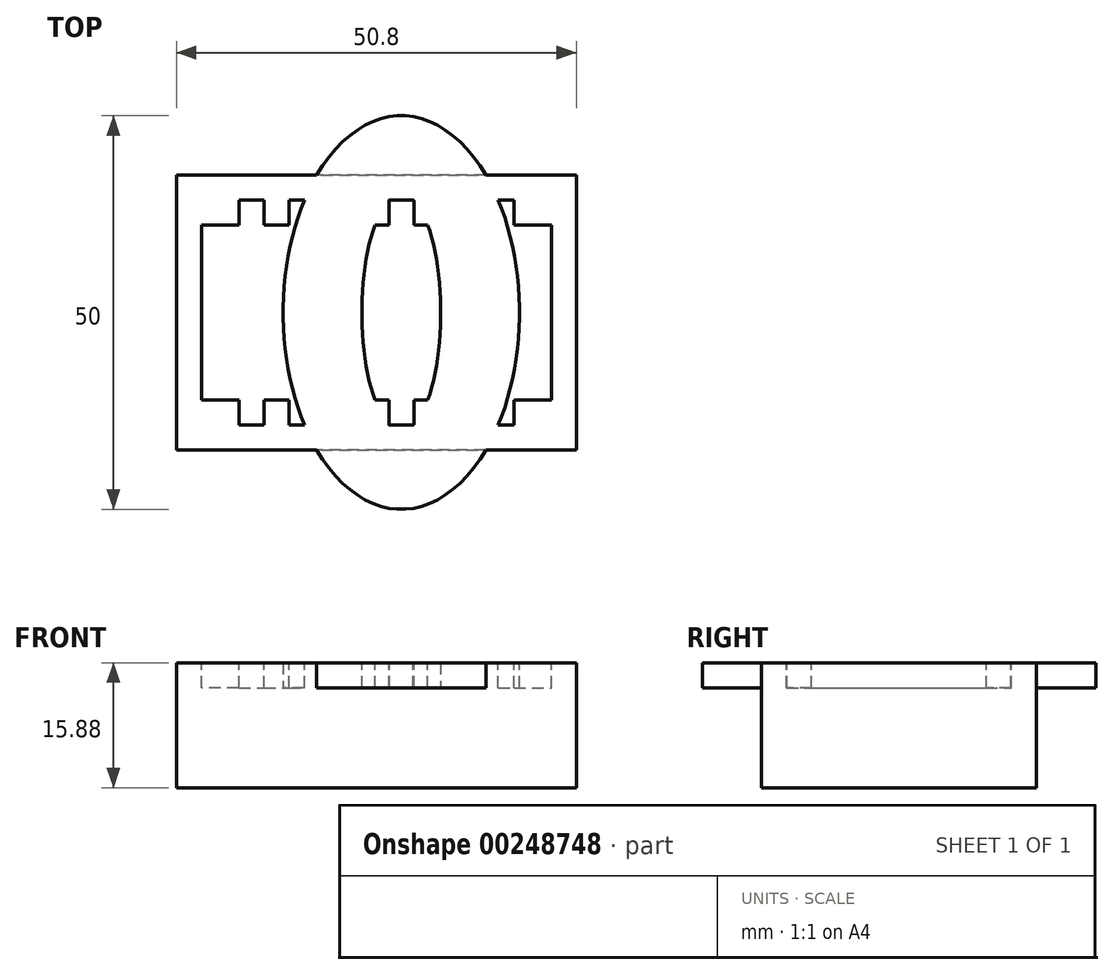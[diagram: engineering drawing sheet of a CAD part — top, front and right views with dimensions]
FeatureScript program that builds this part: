
annotation { "Feature Type Name" : "Feature", "Feature Type Description" : "" }
export const myFeature = defineFeature(function(context is Context, id is Id, definition is map)
    precondition{}
    {
        {
            assignVariable(context, id + "F0", {"name" : "Scale", "anyValue" : 1});
        }
        {
            assignVariable(context, id + "F1", {"name" : "Pixel", "anyValue" : 3.17 * mm});
        }
        {
            var Q0;
            Q0=qCreatedBy(makeId("Top.planeOp"),FACE);
            var sketch = newSketch(context, id + "F2", { "sketchPlane" : qUnion([Q0])});
            skLineSegment(sketch, "E0", {"start": v(-17.46, 14.29) * mm, "end": v(-14.29, 14.29) * mm});
            skLineSegment(sketch, "E1", {"start": v(-14.29, 14.29) * mm, "end": v(-14.29, 11.11) * mm});
            skLineSegment(sketch, "E2", {"start": v(-14.29, 11.11) * mm, "end": v(-11.11, 11.11) * mm});
            skLineSegment(sketch, "E3", {"start": v(-11.11, 11.11) * mm, "end": v(-11.11, 14.29) * mm});
            skLineSegment(sketch, "E4", {"start": v(-11.11, 14.29) * mm, "end": v(-7.94, 14.29) * mm});
            skLineSegment(sketch, "E5", {"start": v(-7.94, 14.29) * mm, "end": v(-7.94, 11.11) * mm});
            skLineSegment(sketch, "E6", {"start": v(-7.94, 11.11) * mm, "end": v(-4.76, 11.11) * mm});
            skLineSegment(sketch, "E7", {"start": v(-4.76, 11.11) * mm, "end": v(-4.76, 14.29) * mm});
            skLineSegment(sketch, "E8", {"start": v(-4.76, 14.29) * mm, "end": v(-1.59, 14.29) * mm});
            skLineSegment(sketch, "E9", {"start": v(-1.59, 14.29) * mm, "end": v(-1.59, 11.11) * mm});
            skLineSegment(sketch, "E10", {"start": v(-1.59, 11.11) * mm, "end": v(1.59, 11.11) * mm});
            skLineSegment(sketch, "E11", {"start": v(1.59, 11.11) * mm, "end": v(1.59, 14.29) * mm});
            skLineSegment(sketch, "E12", {"start": v(1.59, 14.29) * mm, "end": v(4.76, 14.29) * mm});
            skLineSegment(sketch, "E13", {"start": v(4.76, 14.29) * mm, "end": v(4.76, 11.11) * mm});
            skLineSegment(sketch, "E14", {"start": v(4.76, 11.11) * mm, "end": v(7.94, 11.11) * mm});
            skLineSegment(sketch, "E15", {"start": v(7.94, 11.11) * mm, "end": v(7.94, 14.29) * mm});
            skLineSegment(sketch, "E16", {"start": v(7.94, 14.29) * mm, "end": v(11.11, 14.29) * mm});
            skLineSegment(sketch, "E17", {"start": v(11.11, 14.29) * mm, "end": v(11.11, 11.11) * mm});
            skLineSegment(sketch, "E18", {"start": v(11.11, 11.11) * mm, "end": v(14.29, 11.11) * mm});
            skLineSegment(sketch, "E19", {"start": v(14.29, 11.11) * mm, "end": v(14.29, 14.29) * mm});
            skLineSegment(sketch, "E20", {"start": v(14.29, 14.29) * mm, "end": v(17.46, 14.29) * mm});
            skLineSegment(sketch, "E21", {"start": v(17.46, 14.29) * mm, "end": v(17.46, 11.11) * mm});
            skLineSegment(sketch, "E22", {"start": v(17.46, 11.11) * mm, "end": v(22.23, 11.11) * mm});
            skLineSegment(sketch, "E23", {"start": v(-17.46, 14.29) * mm, "end": v(-17.46, 11.11) * mm});
            skLineSegment(sketch, "E24", {"start": v(-17.46, 11.11) * mm, "end": v(-22.23, 11.11) * mm});
            skLineSegment(sketch, "E25", {"start": v(-22.23, 11.11) * mm, "end": v(-22.23, -11.11) * mm});
            skLineSegment(sketch, "E26", {"start": v(-22.23, -11.11) * mm, "end": v(-17.46, -11.11) * mm});
            skLineSegment(sketch, "E27", {"start": v(-17.46, -11.11) * mm, "end": v(-17.46, -14.29) * mm});
            skLineSegment(sketch, "E28", {"start": v(-17.46, -14.29) * mm, "end": v(-14.29, -14.29) * mm});
            skLineSegment(sketch, "E29", {"start": v(-14.29, -14.29) * mm, "end": v(-14.29, -11.11) * mm});
            skLineSegment(sketch, "E30", {"start": v(-14.29, -11.11) * mm, "end": v(-11.11, -11.11) * mm});
            skLineSegment(sketch, "E31", {"start": v(-11.11, -11.11) * mm, "end": v(-11.11, -14.29) * mm});
            skLineSegment(sketch, "E32", {"start": v(-11.11, -14.29) * mm, "end": v(-7.94, -14.29) * mm});
            skLineSegment(sketch, "E33", {"start": v(-7.94, -14.29) * mm, "end": v(-7.94, -11.11) * mm});
            skLineSegment(sketch, "E34", {"start": v(-7.94, -11.11) * mm, "end": v(-4.76, -11.11) * mm});
            skLineSegment(sketch, "E35", {"start": v(-4.76, -11.11) * mm, "end": v(-4.76, -14.29) * mm});
            skLineSegment(sketch, "E36", {"start": v(-4.76, -14.29) * mm, "end": v(-1.59, -14.29) * mm});
            skLineSegment(sketch, "E37", {"start": v(-1.59, -14.29) * mm, "end": v(-1.59, -11.11) * mm});
            skLineSegment(sketch, "E38", {"start": v(-1.59, -11.11) * mm, "end": v(1.59, -11.11) * mm});
            skLineSegment(sketch, "E39", {"start": v(1.59, -11.11) * mm, "end": v(1.59, -14.29) * mm});
            skLineSegment(sketch, "E40", {"start": v(1.59, -14.29) * mm, "end": v(4.76, -14.29) * mm});
            skLineSegment(sketch, "E41", {"start": v(4.76, -14.29) * mm, "end": v(4.76, -11.11) * mm});
            skLineSegment(sketch, "E42", {"start": v(4.76, -11.11) * mm, "end": v(7.94, -11.11) * mm});
            skLineSegment(sketch, "E43", {"start": v(7.94, -11.11) * mm, "end": v(7.94, -14.29) * mm});
            skLineSegment(sketch, "E44", {"start": v(7.94, -14.29) * mm, "end": v(11.11, -14.29) * mm});
            skLineSegment(sketch, "E45", {"start": v(11.11, -14.29) * mm, "end": v(11.11, -11.11) * mm});
            skLineSegment(sketch, "E46", {"start": v(11.11, -11.11) * mm, "end": v(14.29, -11.11) * mm});
            skLineSegment(sketch, "E47", {"start": v(14.29, -11.11) * mm, "end": v(14.29, -14.29) * mm});
            skLineSegment(sketch, "E48", {"start": v(14.29, -14.29) * mm, "end": v(17.46, -14.29) * mm});
            skLineSegment(sketch, "E49", {"start": v(17.46, -14.29) * mm, "end": v(17.46, -11.11) * mm});
            skLineSegment(sketch, "E50", {"start": v(17.46, -11.11) * mm, "end": v(22.23, -11.11) * mm});
            skLineSegment(sketch, "E51", {"start": v(22.23, -11.11) * mm, "end": v(22.23, 11.11) * mm});
            skSolve(sketch);
        }
        {
            var Q0;
            Q0=qCreatedBy(makeId("Top.planeOp"),FACE);
            var sketch = newSketch(context, id + "F3", { "sketchPlane" : qUnion([Q0])});
            skLineSegment(sketch, "E52.bottom", {"start": v(-7.94, 7.94) * mm, "end": v(-4.76, 7.94) * mm});
            skLineSegment(sketch, "E52.top", {"start": v(-7.94, -7.94) * mm, "end": v(-4.76, -7.94) * mm});
            skLineSegment(sketch, "E52.left", {"start": v(-7.94, 7.94) * mm, "end": v(-7.94, -7.94) * mm});
            skLineSegment(sketch, "E52.right", {"start": v(-4.76, 7.94) * mm, "end": v(-4.76, -7.94) * mm});
            skEllipse(sketch, "E53", {"center": v(3.18, 0) * mm, "majorRadius": 25 * mm, "minorRadius": 15 * mm, "majorAxis": v(0, -1)});
            skEllipse(sketch, "E54", {"center": v(3.18, 0) * mm, "majorRadius": 15 * mm, "minorRadius": 5 * mm, "majorAxis": v(0, -1)});
            skPoint(sketch, "E55.endSnap0", {"position": v(3.18, 7.94) * mm});
            skLineSegment(sketch, "E56", {"start": v(-7.94, 0) * mm, "end": v(7.94, 0) * mm, "construction": true});
            skSolve(sketch);
        }
        {
            var Q0;
            Q0=qCreatedBy(makeId("Top.planeOp"),FACE);
            var sketch = newSketch(context, id + "F4", { "sketchPlane" : qUnion([Q0])});
            skLineSegment(sketch, "E57.bottom", {"start": v(-25.4, 17.46) * mm, "end": v(25.4, 17.46) * mm});
            skLineSegment(sketch, "E57.top", {"start": v(-25.4, -17.46) * mm, "end": v(25.4, -17.46) * mm});
            skLineSegment(sketch, "E57.left", {"start": v(-25.4, 17.46) * mm, "end": v(-25.4, -17.46) * mm});
            skLineSegment(sketch, "E57.right", {"start": v(25.4, 17.46) * mm, "end": v(25.4, -17.46) * mm});
            skSolve(sketch);
        }
        {
            var Q0;
            Q0=makeQuery(id+"F4.imprint","IMPRINT",FACE,{"disambiguationData":[TD([[makeQuery(id+"F4.imprint","IMPRINT",EDGE,{"derivedFrom":sQuery(id+"F4.wireOp",EDGE,"E57.bottom")}),-1.0]])]});
            extrude(context, id + "F5", {"entities" : qUnion([Q0]), "oppositeDirection" : true, "depth" : 5 * getVariable(context, 'Pixel')});
        }
        {
            var Q0;
            Q0=makeQuery(id+"F2.imprint","IMPRINT",FACE,{"disambiguationData":[TD([[makeQuery(id+"F2.imprint","IMPRINT",EDGE,{"derivedFrom":sQuery(id+"F2.wireOp",EDGE,"E0")}),-1.0]])]});
            extrude(context, id + "F6", {"entities" : qUnion([Q0]), "operationType" : NewBodyOperationType.REMOVE, "oppositeDirection" : true, "depth" : getVariable(context, 'Scale') * getVariable(context, 'Pixel')});
        }
        {
            var Q0;
            Q0=makeQuery(id+"F3.imprint","IMPRINT",FACE,{"disambiguationData":[TD([[makeQuery(id+"F3.imprint","IMPRINT",EDGE,{"derivedFrom":sQuery(id+"F3.wireOp",EDGE,"E52.bottom")}),-1.0]])]});
            var Q1;
            Q1=makeQuery(id+"F3.imprint","IMPRINT",FACE,{"disambiguationData":[TD([[makeQuery(id+"F3.imprint","IMPRINT",EDGE,{"derivedFrom":sQuery(id+"F3.wireOp",EDGE,"E53")}),1.0]])]});
            extrude(context, id + "F7", {"entities" : qUnion([Q0, Q1]), "operationType" : NewBodyOperationType.ADD, "oppositeDirection" : true, "depth" : getVariable(context, 'Pixel')});
        }
    });
